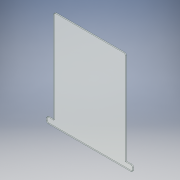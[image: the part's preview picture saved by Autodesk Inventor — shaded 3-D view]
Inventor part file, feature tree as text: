
AUTODESK INVENTOR PART (.ipt)
format: ipt  version: 2019 (Build 230136000, 136)  size: 114,688 bytes
history: native  units: mm
features: extrude x1, fillet x1, sketch x1
ambient origin geometry x8: Origin, YZ Plane, XZ Plane, XY Plane, X Axis, Y Axis, Z Axis, Center Point
bodies: Solid1 (feature_tree)
feature tree (3):
  extrude  "Extrusion1"  Depth=25.0mm
  fillet  "Fillet1"  Radius=300.0mm
  sketch  "Sketch1"  dims[d0=250.0mm d2=25.0mm d3=300.0mm d4=3.5mm d5=0.0mm d6=6.0mm d7=325.0mm d8=20.0mm]
